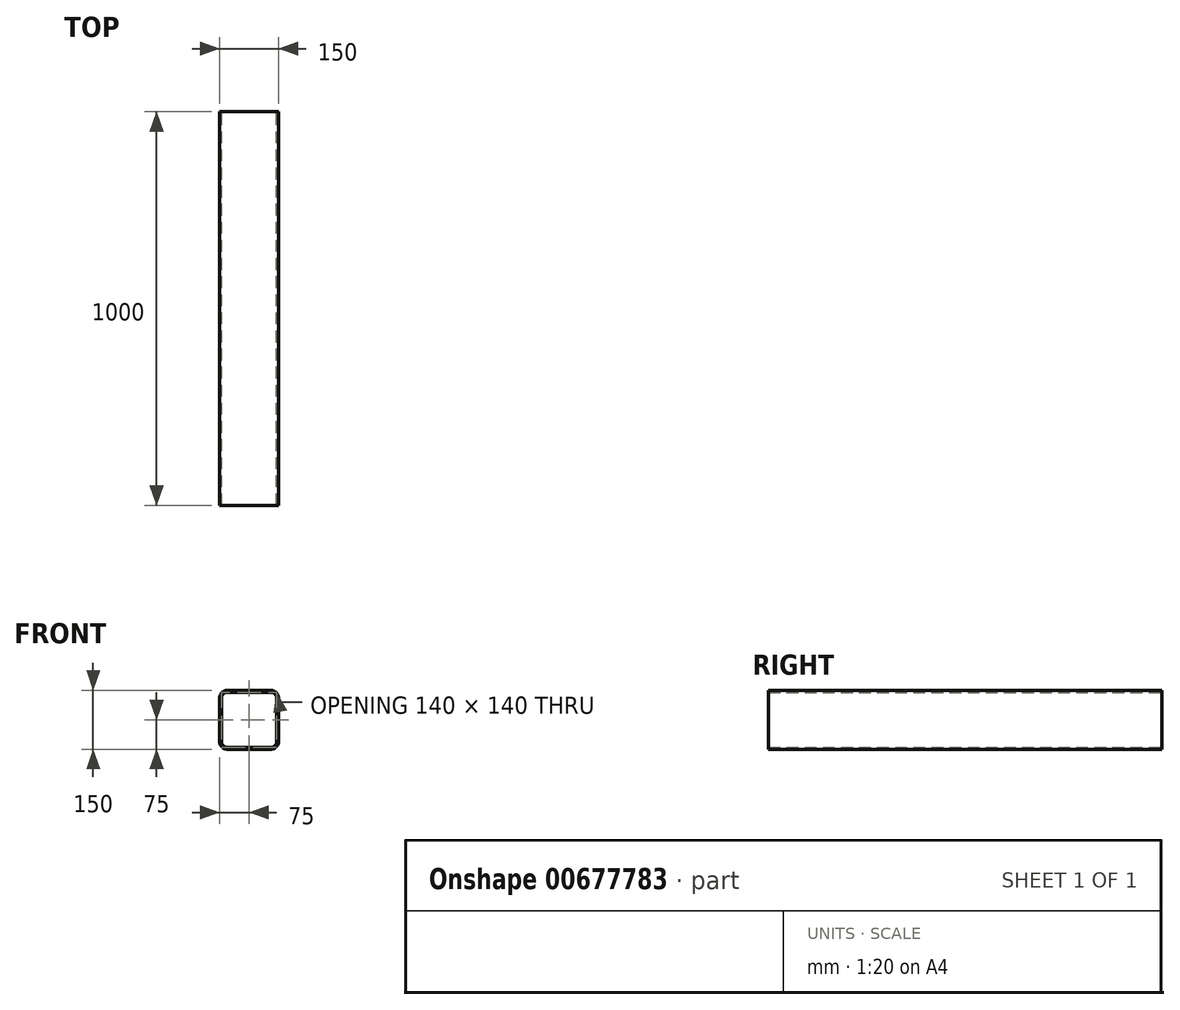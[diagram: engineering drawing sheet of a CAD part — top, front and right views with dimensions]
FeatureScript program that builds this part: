
annotation { "Feature Type Name" : "Feature", "Feature Type Description" : "" }
export const myFeature = defineFeature(function(context is Context, id is Id, definition is map)
    precondition{}
    {
        {
            var Q0;
            Q0=qCreatedBy(makeId("Front.planeOp"),FACE);
            var sketch = newSketch(context, id + "F0", { "sketchPlane" : qUnion([Q0])});
            skLineSegment(sketch, "E0.bottom", {"start": v(55, -75) * mm, "end": v(-55, -75) * mm});
            skLineSegment(sketch, "E0.top", {"start": v(55, 75) * mm, "end": v(-55, 75) * mm});
            skLineSegment(sketch, "E0.left", {"start": v(75, -55) * mm, "end": v(75, 55) * mm});
            skLineSegment(sketch, "E0.right", {"start": v(-75, -55) * mm, "end": v(-75, 55) * mm});
            skPoint(sketch, "E0.middle", {"position": v(0, 0) * mm});
            skPoint(sketch, "E1.visualSharp", {"position": v(-75, 75) * mm});
            skArc(sketch, "E1.filletArc", {"start": v(-55, 75) * mm, "mid": v(-69.14, 69.14) * mm, "end": v(-75, 55) * mm});
            skPoint(sketch, "E2.visualSharp", {"position": v(-75, -75) * mm});
            skArc(sketch, "E2.filletArc", {"start": v(-75, -55) * mm, "mid": v(-69.14, -69.14) * mm, "end": v(-55, -75) * mm});
            skPoint(sketch, "E3.visualSharp", {"position": v(75, -75) * mm});
            skArc(sketch, "E3.filletArc", {"start": v(55, -75) * mm, "mid": v(69.14, -69.14) * mm, "end": v(75, -55) * mm});
            skPoint(sketch, "E4.visualSharp", {"position": v(75, 75) * mm});
            skArc(sketch, "E4.filletArc", {"start": v(75, 55) * mm, "mid": v(69.14, 69.14) * mm, "end": v(55, 75) * mm});
            skArc(sketch, "E5.0", {"start": v(55, -70) * mm, "mid": v(65.6, -65.6) * mm, "end": v(70, -55) * mm});
            skLineSegment(sketch, "E5.1", {"start": v(55, -70) * mm, "end": v(-55, -70) * mm});
            skLineSegment(sketch, "E5.2", {"start": v(70, -55) * mm, "end": v(70, 55) * mm});
            skArc(sketch, "E5.3", {"start": v(-70, -55) * mm, "mid": v(-65.6, -65.6) * mm, "end": v(-55, -70) * mm});
            skArc(sketch, "E5.4", {"start": v(70, 55) * mm, "mid": v(65.6, 65.6) * mm, "end": v(55, 70) * mm});
            skLineSegment(sketch, "E5.5", {"start": v(55, 70) * mm, "end": v(-55, 70) * mm});
            skArc(sketch, "E5.6", {"start": v(-55, 70) * mm, "mid": v(-65.6, 65.6) * mm, "end": v(-70, 55) * mm});
            skLineSegment(sketch, "E5.7", {"start": v(-70, -55) * mm, "end": v(-70, 55) * mm});
            skSolve(sketch);
        }
        {
            var Q0;
            Q0=makeQuery(id+"F0.imprint","IMPRINT",FACE,{"disambiguationData":[TD([[makeQuery(id+"F0.imprint","IMPRINT",EDGE,{"derivedFrom":sQuery(id+"F0.wireOp",EDGE,"E0.bottom")}),-1.0]])]});
            extrude(context, id + "F1", {"entities" : qUnion([Q0]), "depth" : 1000 * mm, "offsetDistance" : 25 * mm});
        }
    });
